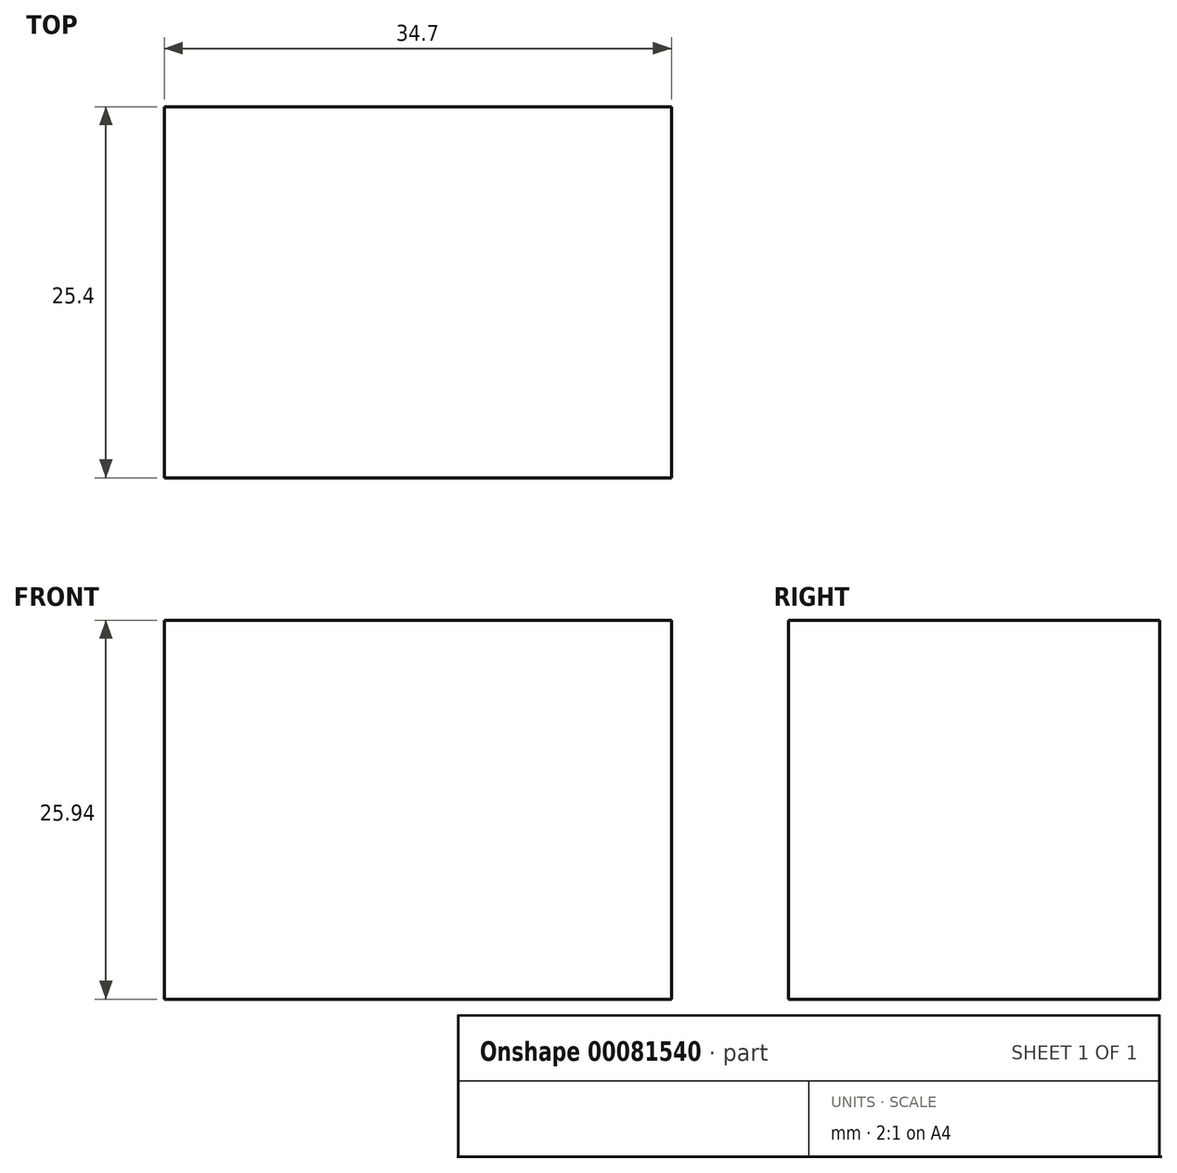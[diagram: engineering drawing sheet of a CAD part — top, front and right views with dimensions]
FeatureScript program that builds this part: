
annotation { "Feature Type Name" : "Feature", "Feature Type Description" : "" }
export const myFeature = defineFeature(function(context is Context, id is Id, definition is map)
    precondition{}
    {
        {
            var Q0;
            Q0=qCreatedBy(makeId("Front.planeOp"),FACE);
            var sketch = newSketch(context, id + "F0", { "sketchPlane" : qUnion([Q0])});
            skLineSegment(sketch, "E0.bottom", {"start": v(-50.05, 51.09) * mm, "end": v(-15.35, 51.09) * mm});
            skLineSegment(sketch, "E0.top", {"start": v(-50.05, 25.15) * mm, "end": v(-15.35, 25.15) * mm});
            skLineSegment(sketch, "E0.left", {"start": v(-50.05, 51.09) * mm, "end": v(-50.05, 25.15) * mm});
            skLineSegment(sketch, "E0.right", {"start": v(-15.35, 51.09) * mm, "end": v(-15.35, 25.15) * mm});
            skSolve(sketch);
        }
        {
            var Q0;
            Q0=makeQuery(id+"F0.imprint","IMPRINT",FACE,{"disambiguationData":[TD([[makeQuery(id+"F0.imprint","IMPRINT",EDGE,{"derivedFrom":sQuery(id+"F0.wireOp",EDGE,"E0.bottom")}),-1.0]])]});
            extrude(context, id + "F1", {"entities" : qUnion([Q0]), "depth" : 25.4 * mm});
        }
    });
